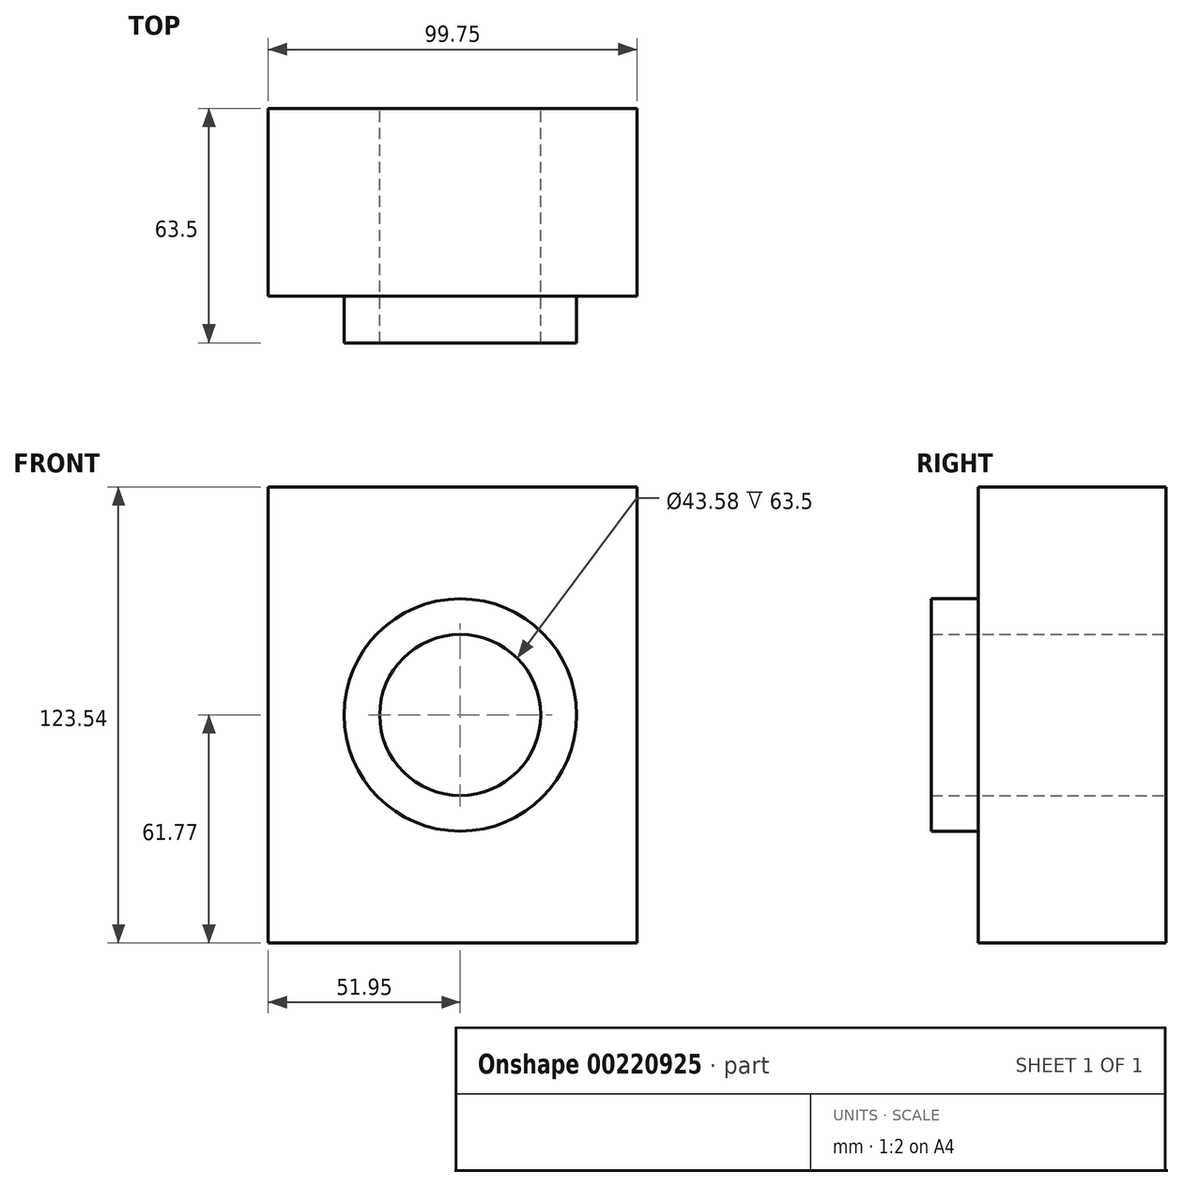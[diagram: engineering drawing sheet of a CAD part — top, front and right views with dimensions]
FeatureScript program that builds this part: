
annotation { "Feature Type Name" : "Feature", "Feature Type Description" : "" }
export const myFeature = defineFeature(function(context is Context, id is Id, definition is map)
    precondition{}
    {
        {
            var Q0;
            Q0=qCreatedBy(makeId("Front.planeOp"),FACE);
            var sketch = newSketch(context, id + "F0", { "sketchPlane" : qUnion([Q0])});
            skLineSegment(sketch, "E0.bottom", {"start": v(-51.95, 61.77) * mm, "end": v(47.8, 61.77) * mm});
            skLineSegment(sketch, "E0.top", {"start": v(-51.95, -61.77) * mm, "end": v(47.8, -61.77) * mm});
            skLineSegment(sketch, "E0.left", {"start": v(-51.95, 61.77) * mm, "end": v(-51.95, -61.77) * mm});
            skLineSegment(sketch, "E0.right", {"start": v(47.8, 61.77) * mm, "end": v(47.8, -61.77) * mm});
            skPoint(sketch, "E0.middle", {"position": v(-2.08, 0) * mm});
            skCircle(sketch, "E1", {"center": v(0, 0) * mm, "radius": 31.46 * mm});
            skCircle(sketch, "E2", {"center": v(0, 0) * mm, "radius": 21.79 * mm});
            skSolve(sketch);
        }
        {
            var Q0;
            Q0=makeQuery(id+"F0.imprint","IMPRINT",FACE,{"disambiguationData":[TD([[makeQuery(id+"F0.imprint","IMPRINT",EDGE,{"derivedFrom":sQuery(id+"F0.wireOp",EDGE,"E0.bottom")}),-1.0]])]});
            extrude(context, id + "F1", {"entities" : qUnion([Q0]), "depth" : 50.8 * mm});
        }
        {
            var Q0;
            Q0=makeQuery(id+"F0.imprint","IMPRINT",FACE,{"disambiguationData":[TD([[makeQuery(id+"F0.imprint","IMPRINT",EDGE,{"derivedFrom":sQuery(id+"F0.wireOp",EDGE,"E1")}),1.0]])]});
            extrude(context, id + "F2", {"entities" : qUnion([Q0]), "operationType" : NewBodyOperationType.ADD, "depth" : 63.5 * mm});
        }
    });
